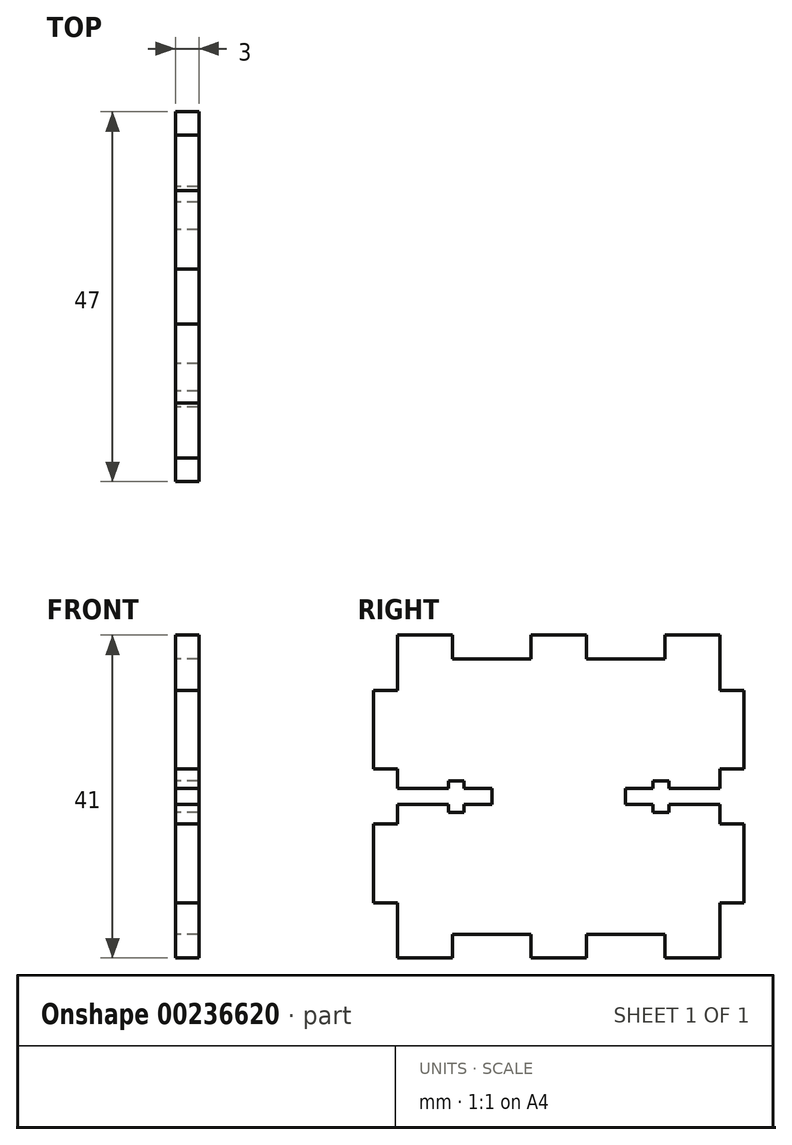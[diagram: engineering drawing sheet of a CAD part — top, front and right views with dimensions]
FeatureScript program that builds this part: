
annotation { "Feature Type Name" : "Feature", "Feature Type Description" : "" }
export const myFeature = defineFeature(function(context is Context, id is Id, definition is map)
    precondition{}
    {
        {
            var Q0;
            Q0=qCreatedBy(makeId("Right.planeOp"),FACE);
            var sketch = newSketch(context, id + "F0", { "sketchPlane" : qUnion([Q0])});
            skLineSegment(sketch, "E0", {"start": v(24, 0) * mm, "end": v(24, 3) * mm});
            skLineSegment(sketch, "E1", {"start": v(24, 3) * mm, "end": v(34, 3) * mm});
            skLineSegment(sketch, "E2", {"start": v(41, 7) * mm, "end": v(44, 7) * mm});
            skLineSegment(sketch, "E3", {"start": v(44, 7) * mm, "end": v(44, 17) * mm});
            skLineSegment(sketch, "E4", {"start": v(44, 17) * mm, "end": v(41, 17) * mm});
            skLineSegment(sketch, "E5", {"start": v(41, 17) * mm, "end": v(41, 19.5) * mm});
            skLineSegment(sketch, "E6", {"start": v(41, 19.5) * mm, "end": v(34.5, 19.5) * mm});
            skLineSegment(sketch, "E7", {"start": v(34.5, 19.5) * mm, "end": v(34.5, 18.5) * mm});
            skLineSegment(sketch, "E8", {"start": v(34.5, 18.5) * mm, "end": v(32.5, 18.5) * mm});
            skLineSegment(sketch, "E9", {"start": v(32.5, 18.5) * mm, "end": v(32.5, 19.5) * mm});
            skLineSegment(sketch, "E10", {"start": v(32.5, 19.5) * mm, "end": v(29, 19.5) * mm});
            skLineSegment(sketch, "E11", {"start": v(29, 19.5) * mm, "end": v(29, 20.5) * mm});
            skLineSegment(sketch, "E12", {"start": v(44.49, 20.5) * mm, "end": v(0, 20.5) * mm, "construction": true});
            skLineSegment(sketch, "E13", {"start": v(20.5, 0) * mm, "end": v(24, 0) * mm});
            skLineSegment(sketch, "E14", {"start": v(20.5, 41) * mm, "end": v(20.5, 0) * mm, "construction": true});
            skLineSegment(sketch, "E15", {"start": v(34, 3) * mm, "end": v(34, 0) * mm});
            skLineSegment(sketch, "E16", {"start": v(34, 0) * mm, "end": v(41, 0) * mm});
            skLineSegment(sketch, "E17", {"start": v(41, 0) * mm, "end": v(41, 7) * mm});
            skLineSegment(sketch, "E18.MirrorCS", {"start": v(34.5, 22.5) * mm, "end": v(32.5, 22.5) * mm});
            skLineSegment(sketch, "E19.MirrorCS", {"start": v(41, 34) * mm, "end": v(44, 34) * mm});
            skLineSegment(sketch, "E20.MirrorCS", {"start": v(29, 21.5) * mm, "end": v(29, 20.5) * mm});
            skLineSegment(sketch, "E21.MirrorCS", {"start": v(41, 24) * mm, "end": v(41, 21.5) * mm});
            skLineSegment(sketch, "E22.MirrorCS", {"start": v(32.5, 22.5) * mm, "end": v(32.5, 21.5) * mm});
            skLineSegment(sketch, "E23.MirrorCS", {"start": v(44, 24) * mm, "end": v(41, 24) * mm});
            skLineSegment(sketch, "E24.MirrorCS", {"start": v(34.5, 21.5) * mm, "end": v(34.5, 22.5) * mm});
            skLineSegment(sketch, "E25.MirrorCS", {"start": v(34, 41) * mm, "end": v(41, 41) * mm});
            skLineSegment(sketch, "E26.MirrorCS", {"start": v(41, 21.5) * mm, "end": v(34.5, 21.5) * mm});
            skLineSegment(sketch, "E27.MirrorCS", {"start": v(41, 41) * mm, "end": v(41, 34) * mm});
            skLineSegment(sketch, "E28.MirrorCS", {"start": v(32.5, 21.5) * mm, "end": v(29, 21.5) * mm});
            skLineSegment(sketch, "E29.MirrorCS", {"start": v(24, 41) * mm, "end": v(24, 38) * mm});
            skLineSegment(sketch, "E30.MirrorCS", {"start": v(24, 38) * mm, "end": v(34, 38) * mm});
            skLineSegment(sketch, "E31.MirrorCS", {"start": v(44, 34) * mm, "end": v(44, 24) * mm});
            skLineSegment(sketch, "E32.MirrorCS", {"start": v(20.5, 41) * mm, "end": v(24, 41) * mm});
            skLineSegment(sketch, "E33.MirrorCS", {"start": v(34, 38) * mm, "end": v(34, 41) * mm});
            skLineSegment(sketch, "E34.MirrorCS", {"start": v(12, 21.5) * mm, "end": v(12, 20.5) * mm});
            skLineSegment(sketch, "E35.MirrorCS", {"start": v(6.5, 19.5) * mm, "end": v(6.5, 18.5) * mm});
            skLineSegment(sketch, "E36.MirrorCS", {"start": v(12, 19.5) * mm, "end": v(12, 20.5) * mm});
            skLineSegment(sketch, "E37.MirrorCS", {"start": v(6.5, 22.5) * mm, "end": v(8.5, 22.5) * mm});
            skLineSegment(sketch, "E38.MirrorCS", {"start": v(6.5, 21.5) * mm, "end": v(6.5, 22.5) * mm});
            skLineSegment(sketch, "E39.MirrorCS", {"start": v(8.5, 21.5) * mm, "end": v(12, 21.5) * mm});
            skLineSegment(sketch, "E40.MirrorCS", {"start": v(8.5, 18.5) * mm, "end": v(8.5, 19.5) * mm});
            skLineSegment(sketch, "E41.MirrorCS", {"start": v(6.5, 18.5) * mm, "end": v(8.5, 18.5) * mm});
            skLineSegment(sketch, "E42.MirrorCS", {"start": v(8.5, 19.5) * mm, "end": v(12, 19.5) * mm});
            skLineSegment(sketch, "E43.MirrorCS", {"start": v(20.5, 0) * mm, "end": v(17, 0) * mm});
            skLineSegment(sketch, "E44.MirrorCS", {"start": v(7, 3) * mm, "end": v(7, 0) * mm});
            skLineSegment(sketch, "E45.MirrorCS", {"start": v(0, 7) * mm, "end": v(-3, 7) * mm});
            skLineSegment(sketch, "E46.MirrorCS", {"start": v(0, 17) * mm, "end": v(0, 19.5) * mm});
            skLineSegment(sketch, "E47.MirrorCS", {"start": v(7, 38) * mm, "end": v(7, 41) * mm});
            skLineSegment(sketch, "E48.MirrorCS", {"start": v(8.5, 22.5) * mm, "end": v(8.5, 21.5) * mm});
            skLineSegment(sketch, "E49.MirrorCS", {"start": v(0, 34) * mm, "end": v(-3, 34) * mm});
            skLineSegment(sketch, "E50.MirrorCS", {"start": v(17, 0) * mm, "end": v(17, 3) * mm});
            skLineSegment(sketch, "E51.MirrorCS", {"start": v(20.5, 41) * mm, "end": v(17, 41) * mm});
            skLineSegment(sketch, "E52.MirrorCS", {"start": v(17, 41) * mm, "end": v(17, 38) * mm});
            skLineSegment(sketch, "E53.MirrorCS", {"start": v(0, 24) * mm, "end": v(0, 21.5) * mm});
            skLineSegment(sketch, "E54.MirrorCS", {"start": v(-3, 24) * mm, "end": v(0, 24) * mm});
            skLineSegment(sketch, "E55.MirrorCS", {"start": v(-3, 17) * mm, "end": v(0, 17) * mm});
            skLineSegment(sketch, "E56.MirrorCS", {"start": v(-3, 34) * mm, "end": v(-3, 24) * mm});
            skLineSegment(sketch, "E57.MirrorCS", {"start": v(17, 38) * mm, "end": v(7, 38) * mm});
            skLineSegment(sketch, "E58.MirrorCS", {"start": v(7, 41) * mm, "end": v(0, 41) * mm});
            skLineSegment(sketch, "E59.MirrorCS", {"start": v(0, 19.5) * mm, "end": v(6.5, 19.5) * mm});
            skLineSegment(sketch, "E60.MirrorCS", {"start": v(0, 21.5) * mm, "end": v(6.5, 21.5) * mm});
            skLineSegment(sketch, "E61.MirrorCS", {"start": v(17, 3) * mm, "end": v(7, 3) * mm});
            skLineSegment(sketch, "E62.MirrorCS", {"start": v(0, 0) * mm, "end": v(0, 7) * mm});
            skLineSegment(sketch, "E63.MirrorCS", {"start": v(7, 0) * mm, "end": v(0, 0) * mm});
            skLineSegment(sketch, "E64.MirrorCS", {"start": v(0, 41) * mm, "end": v(0, 34) * mm});
            skLineSegment(sketch, "E65.MirrorCS", {"start": v(-3, 7) * mm, "end": v(-3, 17) * mm});
            skSolve(sketch);
        }
        {
            var Q0;
            Q0=qSketchRegion(id+"F0",true);
            extrude(context, id + "F1", {"entities" : qUnion([Q0]), "depth" : 3 * mm});
        }
    });
